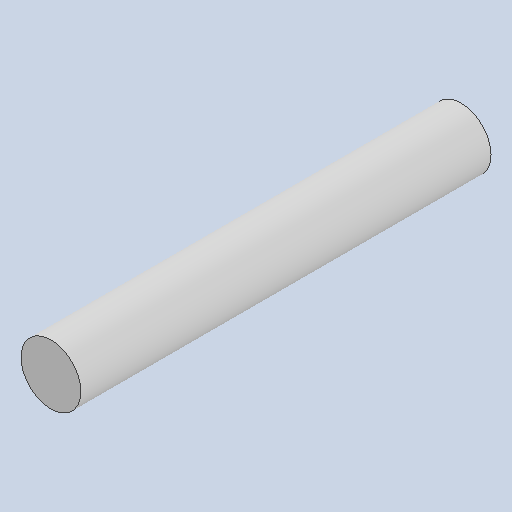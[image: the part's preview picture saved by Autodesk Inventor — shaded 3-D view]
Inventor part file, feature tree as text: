
AUTODESK INVENTOR PART (.ipt)
format: ipt  version: 2024.3 (Build 283343000, 343)  size: 83,968 bytes
history: native  units: mm
features: other x3, sketch x1
ambient origin geometry x8: Origin, YZ Plane, XZ Plane, XY Plane, X Axis, Y Axis, Z Axis, Center Point
bodies: Solid1 (feature_tree)
feature tree (4):
  other  "eje.ipt"
  other  "Solid1::eje.ipt"
  other  "TaggingFeature1"
  sketch  "Sketch1"  dims[d0=10.0mm]
